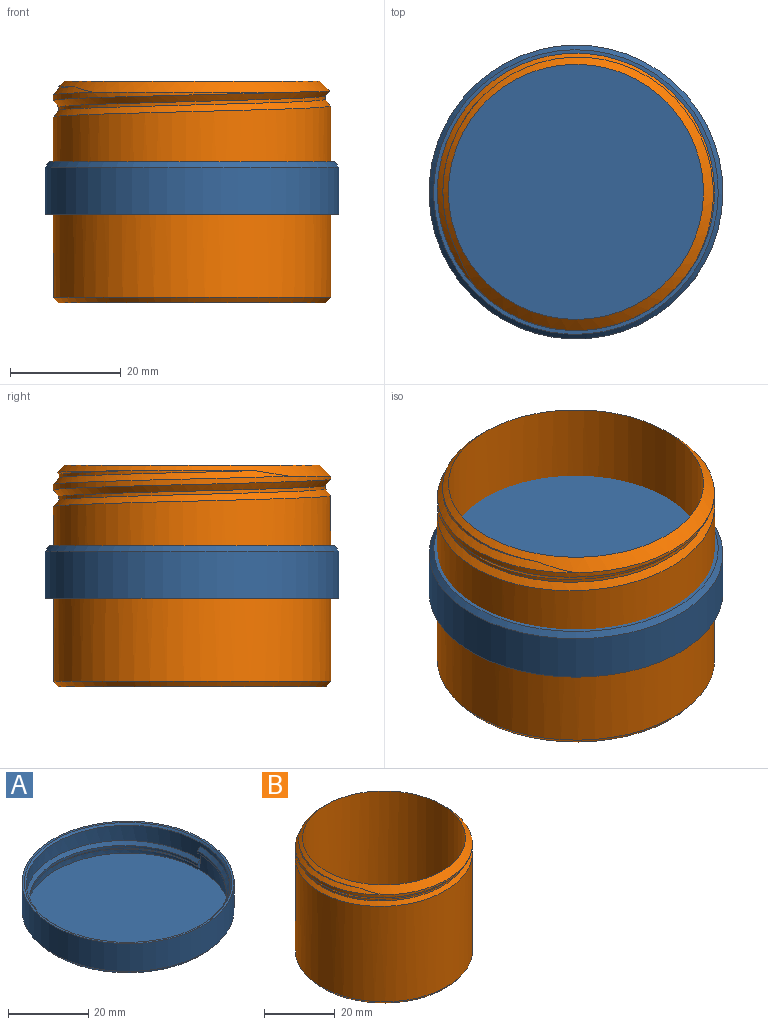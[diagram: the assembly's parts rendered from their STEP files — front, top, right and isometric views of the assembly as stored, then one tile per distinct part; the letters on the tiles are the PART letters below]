
ASSEMBLY  parts=2 mates=1
PART A: 13 faces, bbox 53x58.8x9.5 mm
  f0: cylinder r=26.5mm len=53mm, axis (0,0,-1), area 1415.3mm2, adj f2,f3
  f1: plane 51.32x51.32mm, normal (0,0,-1), area 2068.7mm2, adj f2
  f2: cone r=26.5mm half-angle=40deg, axis (0,0,1), area 213.9mm2, adj f0,f1
  f3: plane 53x53mm, normal (0,0,1), area 90.6mm2, adj f0,f12
  f4: plane 50.9x50.9mm, normal (0,0,1), area 2034.8mm2, adj f11
  f5: plane 2.6x0.8mm, normal (0,-1,0), area 1.3mm2, adj f6,f7,f9,f11
  f6: bspline ~58.77x50.9mm, area 196mm2, adj f5,f7,f8,f11
  f7: cylinder r=24.65mm len=49.3mm, axis (0,0,1), area 107.4mm2, adj f5,f6,f8,f9
  f8: plane 2.6x0.8mm, normal (0,1,0), area 1.3mm2, adj f6,f7,f9,f10
  f9: bspline ~58.77x50.9mm, area 196mm2, adj f5,f7,f8,f10
  f10: cylinder r=25.45mm len=50.9mm, axis (0,0,1), area 511.7mm2, adj f8,f9,f11,f12
  f11: cylinder r=25.45mm len=50.9mm, axis (0,0,1), area 431.7mm2, adj f4,f5,f6,f10
  f12: cone r=25.45mm half-angle=45deg, axis (0,0,1), area 114.2mm2, adj f3,f10
PART B: 12 faces, bbox 50x57.7x40.5 mm
  f0: cylinder r=25mm len=50mm, axis (0,0,-1), area 5105.1mm2, adj f1,f4,f6,f7
  f1: cylinder r=25mm len=50mm, axis (0,0,-1), area 118.6mm2, adj f0,f3,f4,f8
  f2: cylinder r=24mm len=48mm, axis (0,0,1), area 139.5mm2, adj f3,f4,f6,f8
  f3: bspline ~57.74x50mm, area 275mm2, adj f1,f2,f6,f8
  f4: bspline ~57.74x50mm, area 383.2mm2, adj f0,f1,f2,f6,f8
  f5: plane 48.32x48.32mm, normal (0,0,-1), area 1833.9mm2, adj f7
  f6: plane 3x1mm, normal (0,1,0), area 1.8mm2, adj f0,f2,f3,f4
  f7: cone r=25mm half-angle=40deg, axis (0,0,1), area 201.6mm2, adj f0,f5
  f8: cone r=25mm half-angle=45deg, axis (0,0,-1), area 327.9mm2, adj f1,f2,f3,f4,f11
  f9: plane 42x42mm, normal (0,0,1), area 1385.4mm2, adj f10
  f10: torus R=21mm, axis (0,0,1), area 439.7mm2, adj f9,f11
  f11: cylinder r=23mm len=46mm, axis (0,0,1), area 5347mm2, adj f8,f10
PLACE A rot(axis=(-0.28,-0.96,0),180deg) t=(-7.25,-0.74,24.38)mm
PLACE B t=(-7.25,-0.74,-1.09)mm fixed
MATE cylindrical A.f7 <-> B.f8  axis (0,0,-1) through (-7.25,-0.74,23.88)mm
